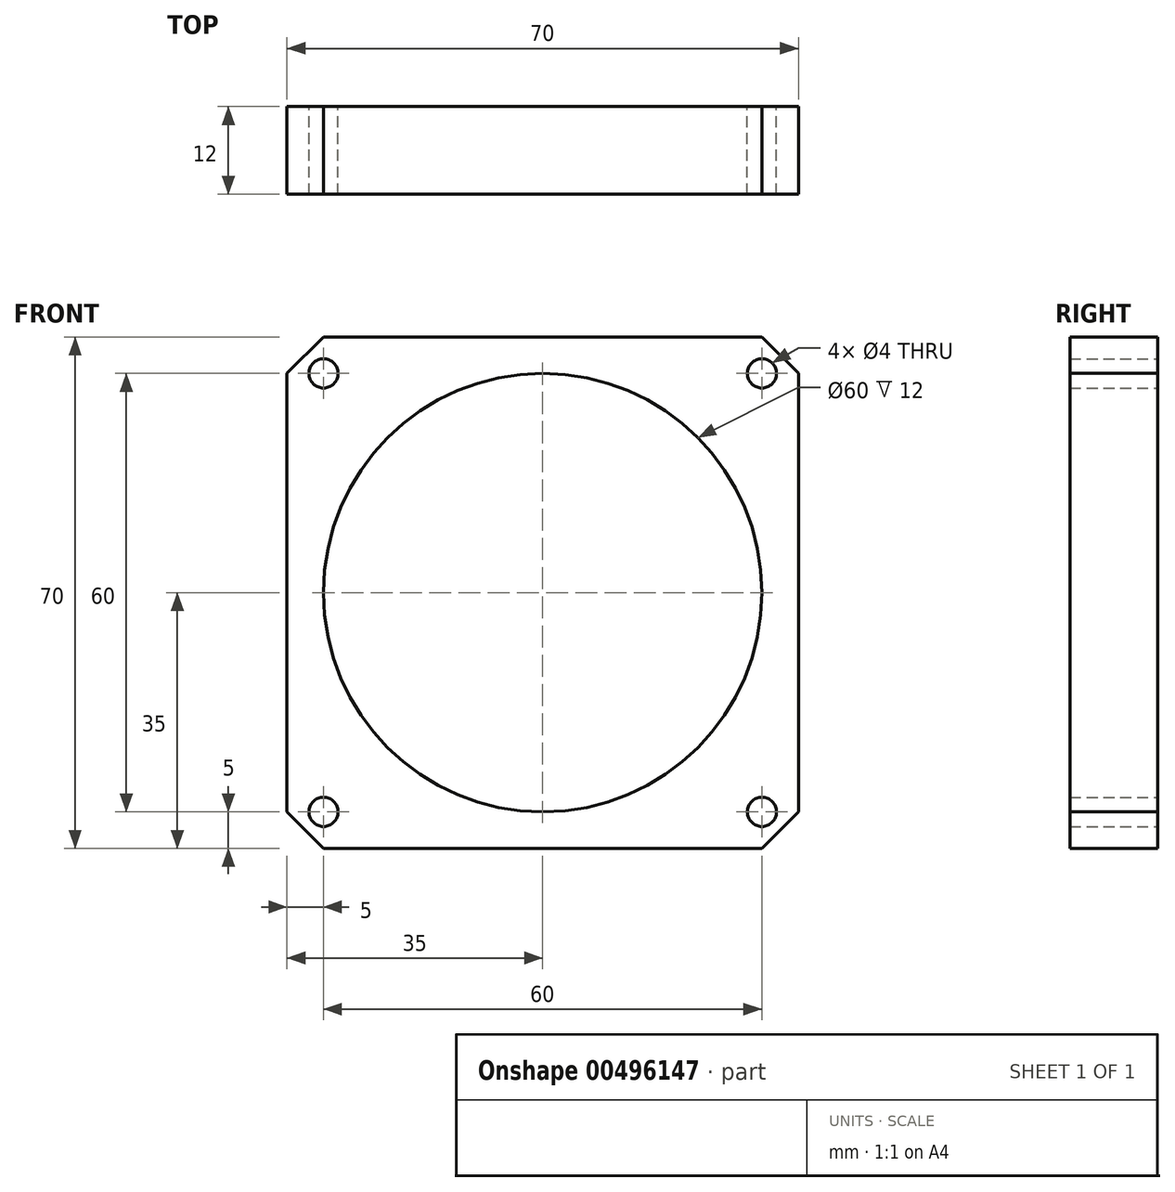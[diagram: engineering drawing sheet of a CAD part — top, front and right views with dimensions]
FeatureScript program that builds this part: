
annotation { "Feature Type Name" : "Feature", "Feature Type Description" : "" }
export const myFeature = defineFeature(function(context is Context, id is Id, definition is map)
    precondition{}
    {
        {
            var Q0;
            Q0=qCreatedBy(makeId("Front.planeOp"),FACE);
            var sketch = newSketch(context, id + "F0", { "sketchPlane" : qUnion([Q0])});
            skLineSegment(sketch, "E0.bottom", {"start": v(35, 35) * mm, "end": v(-35, 35) * mm});
            skLineSegment(sketch, "E0.top", {"start": v(35, -35) * mm, "end": v(-35, -35) * mm});
            skLineSegment(sketch, "E0.left", {"start": v(35, 35) * mm, "end": v(35, -35) * mm});
            skLineSegment(sketch, "E0.right", {"start": v(-35, 35) * mm, "end": v(-35, -35) * mm});
            skPoint(sketch, "E0.middle", {"position": v(0, 0) * mm});
            skCircle(sketch, "E1", {"center": v(0, 0) * mm, "radius": 30 * mm});
            skPoint(sketch, "E2", {"position": v(-30, 30) * mm});
            skPoint(sketch, "E3", {"position": v(30, 30) * mm});
            skPoint(sketch, "E4", {"position": v(30, -30) * mm});
            skPoint(sketch, "E5", {"position": v(-30, -30) * mm});
            skCircle(sketch, "E6", {"center": v(-30, 30) * mm, "radius": 2 * mm});
            skCircle(sketch, "E7", {"center": v(30, 30) * mm, "radius": 2 * mm});
            skCircle(sketch, "E8", {"center": v(30, -30) * mm, "radius": 2 * mm});
            skCircle(sketch, "E9", {"center": v(-30, -30) * mm, "radius": 2 * mm});
            skSolve(sketch);
        }
        {
            var Q0;
            Q0 = qSketchRegion(id + "F0", true);
            extrude(context, id + "F1", {"entities" : qUnion([Q0]), "depth" : 12 * mm});
        }
        {
            var Q0;
            Q0=makeQuery(id+"F1.opExtrude","SWEPT_EDGE",EDGE,{"disambiguationData":[OSD([sQuery(id+"F0.wireOp",EDGE,"E0.bottom"),sQuery(id+"F0.wireOp",EDGE,"E0.right")])]});
            var Q1;
            Q1=makeQuery(id+"F1.opExtrude","SWEPT_EDGE",EDGE,{"disambiguationData":[OSD([sQuery(id+"F0.wireOp",EDGE,"E0.bottom"),sQuery(id+"F0.wireOp",EDGE,"E0.left")])]});
            var Q2;
            Q2=makeQuery(id+"F1.opExtrude","SWEPT_EDGE",EDGE,{"disambiguationData":[OSD([sQuery(id+"F0.wireOp",EDGE,"E0.top"),sQuery(id+"F0.wireOp",EDGE,"E0.left")])]});
            var Q3;
            Q3=makeQuery(id+"F1.opExtrude","SWEPT_EDGE",EDGE,{"disambiguationData":[OSD([sQuery(id+"F0.wireOp",EDGE,"E0.top"),sQuery(id+"F0.wireOp",EDGE,"E0.right")])]});
            chamfer(context, id + "F2", {"entities" : qUnion([Q0, Q1, Q2, Q3]), "width" : 5 * mm, "tangentPropagation" : true});
        }
    });
